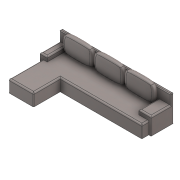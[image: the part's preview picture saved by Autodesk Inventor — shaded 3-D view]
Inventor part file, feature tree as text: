
AUTODESK INVENTOR PART (.ipt)
format: ipt  version: 2020.2 (Build 242310000, 310)  size: 756,736 bytes
history: native  units: mm
features: plane x6, fillet x6, sketch x6, extrude x3, other x1
ambient origin geometry x8: Origin, YZ Plane, XZ Plane, XY Plane, X Axis, Y Axis, Z Axis, Center Point
bodies: Solid1 (feature_tree), Solid7 (feature_tree), Solid8 (feature_tree), Solid9 (feature_tree)
feature tree (22):
  plane  "Work Plane1"
  extrude  "D. Sediste 350"  Depth=750.0mm
  plane  "Work Plane2"
  plane  "Work Plane3"
  fillet  "Fillet4"  Radius=1500.0mm
  plane  "Work Plane4"
  extrude  "Extrusion6"  Depth=75.0mm
  plane  "Work Plane5"
  extrude  "Extrusion7"  Depth=15.0mm TaperAngle=0.0deg
  plane  "Work Plane6"
  other  "Form3"
  fillet  "Fillet5"  Radius=15.0mm
  fillet  "Fillet6"  Radius=85.0mm
  fillet  "Fillet7"  Radius=50.0mm
  fillet  "Fillet8"  Radius=700.0mm
  fillet  "Fillet9"  Radius=1500.0mm
  sketch  "Sketch2"  dims[d1=50.0mm d31=750.0mm d32=1500.0mm]
  sketch  "Sketch3"  dims[d34=50.0mm d35=75.0mm]
  sketch  "Sketch7"  dims[d36=50.0mm d38=15.0mm d39=0.0mm d40=15.0mm d41=85.0mm d42=50.0mm d43=700.0mm d44=1500.0mm]
  sketch  "Sketch8"  dims[d45=350.0mm d46=0.0mm]
  sketch  "Sketch10"  dims[d47=0.0mm]
  sketch  "Sketch11"  dims[d50=0.0mm d51=750.0mm d52=2300.0mm d53=0.0mm d56=50.0mm d61=15.0mm d62=0.0mm d64=20.0mm d65=0.0mm d80=65.0mm d81=350.0mm d82=550.0mm d83=65.0mm d84=200.0mm d85=550.0mm d86=130.0mm d87=350.0mm d88=0.0mm d89=0.0mm d90=0.0mm d91=750.0mm d92=80.0mm d93=0.0mm d94=0.0mm d95=40.0mm d96=20.0mm d97=40.0mm d98=5.0mm d99=2.0mm]
